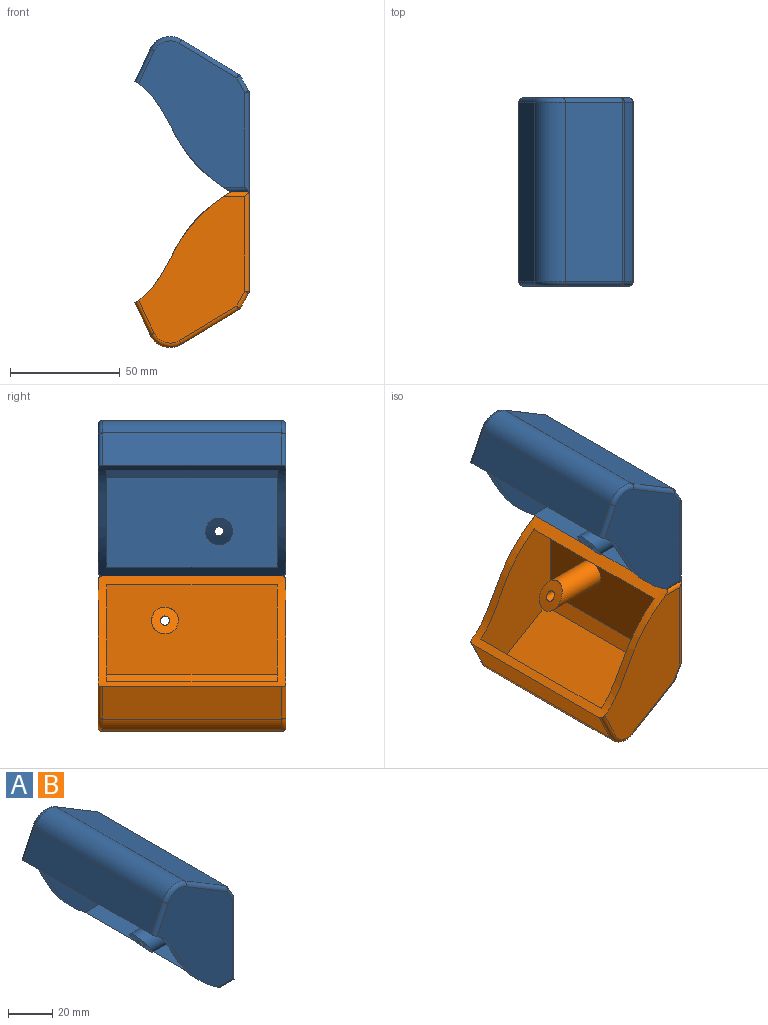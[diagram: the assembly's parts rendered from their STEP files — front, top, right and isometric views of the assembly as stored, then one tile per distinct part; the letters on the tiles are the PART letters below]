
ASSEMBLY  parts=2 mates=1
PART A: 38 faces, bbox 52.8x85.6x72.1 mm
  f0: plane 81.6x6.67mm, normal (0.87,0,0.49), area 624.7mm2, adj f19,f22,f23,f26
  f1: plane 69.24x50.77mm, normal (0,-1,0), area 1975.9mm2, adj f14,f15,f16,f17,f18,f26,f28
  f2: plane 69.24x50.77mm, normal (0,1,0), area 1975.9mm2, adj f9,f10,f11,f12,f13,f19,f28
  f3: plane 81.6x14.69mm, normal (-0.9,0,0.43), area 1328.2mm2, adj f8,f13,f18,f28
  f4: plane 81.6x8.33mm, normal (0,0,-1), area 679.4mm2, adj f5,f12,f17,f28
  f5: plane 81.6x45.27mm, normal (1,0,0), area 3680.4mm2, adj f4,f7,f10,f15,f23
  f6: plane 81.6x26.14mm, normal (0.52,0,0.86), area 2490.6mm2, adj f8,f9,f14,f22
  f7: cylinder r=2.1mm len=31.51mm, axis (1,0,0), area 397.6mm2, adj f5,f27
  f8: cylinder r=10mm len=81.6mm, axis (0,1,0), area 1360.6mm2, adj f3,f6,f11,f16
  f9: cylinder r=2mm len=27.17mm, axis (-0.86,0,0.52), area 95.9mm2, adj f2,f6,f11,f20
  f10: cylinder r=2mm len=45.27mm, axis (0,0,1), area 139.9mm2, adj f2,f5,f12,f21
  f11: torus R=8mm, axis (0,-1,0), area 48.6mm2, adj f2,f8,f9,f13
  f12: cylinder r=2mm len=11.6mm, axis (1,0,0), area 27.7mm2, adj f2,f4,f10,f28
  f13: cylinder r=2mm len=15.74mm, axis (-0.43,0,-0.9), area 51.5mm2, adj f2,f3,f11,f28
  f14: cylinder r=2mm len=27.17mm, axis (0.86,0,-0.52), area 95.9mm2, adj f1,f6,f16,f24
  f15: cylinder r=2mm len=45.27mm, axis (0,0,-1), area 139.9mm2, adj f1,f5,f17,f25
  f16: torus R=8mm, axis (0,-1,0), area 48.6mm2, adj f1,f8,f14,f18
  f17: cylinder r=2mm len=11.6mm, axis (-1,0,0), area 27.7mm2, adj f1,f4,f15,f28
  f18: cylinder r=2mm len=15.74mm, axis (0.43,0,0.9), area 51.5mm2, adj f1,f3,f16,f28
  f19: cylinder r=2mm len=7.65mm, axis (-0.49,0,0.87), area 24mm2, adj f0,f2,f20,f21
  f20: sphere r=2mm, area 2.1mm2, adj f9,f19,f22
  f21: sphere r=2mm, area 2.1mm2, adj f10,f19,f23
  f22: cylinder r=2mm len=81.6mm, axis (0,1,0), area 83.9mm2, adj f0,f6,f20,f24
  f23: cylinder r=2mm len=81.6mm, axis (0,-1,0), area 83.9mm2, adj f0,f5,f21,f25
  f24: sphere r=2mm, area 2.1mm2, adj f14,f22,f26
  f25: sphere r=2mm, area 2.1mm2, adj f15,f23,f26
  f26: cylinder r=2mm len=7.65mm, axis (-0.49,0,0.87), area 24mm2, adj f0,f1,f24,f25
  f27: extruded ~12.2x12.2mm, area 124.6mm2, adj f7,f30
  f28: extruded ~85.6x50.47mm, area 1425.1mm2, adj f1,f2,f3,f4,f12,f13,f17,f18
  f29: cylinder r=6mm len=77.6mm, axis (0,1,0), area 776.3mm2, adj f31,f34,f35,f36
  f30: cylinder r=6.1mm len=29.87mm, axis (1,0,0), area 994.5mm2, adj f27,f32
  f31: plane 77.6x25.69mm, normal (-0.52,0,-0.86), area 2327.7mm2, adj f29,f35,f36,f37
  f32: plane 77.6x40.75mm, normal (-1,0,0), area 3045.1mm2, adj f30,f33,f35,f36,f37
  f33: plane 77.6x10.53mm, normal (0,0,1), area 817.3mm2, adj f28,f32,f35,f36
  f34: plane 77.6x15.21mm, normal (0.9,0,-0.43), area 1308.3mm2, adj f28,f29,f35,f36
  f35: plane 64.75x46.63mm, normal (0,-1,0), area 1740.3mm2, adj f28,f29,f31,f32,f33,f34,f37
  f36: plane 64.75x46.63mm, normal (0,1,0), area 1740.3mm2, adj f28,f29,f31,f32,f33,f34,f37
  f37: plane 77.6x5.75mm, normal (-0.87,0,-0.49), area 512.4mm2, adj f31,f32,f35,f36
PART B: same geometry as A
PLACE A t=(-33.89,38.05,-9.02)mm fixed
PLACE B rot(axis=(1,0,0),180deg) t=(-33.89,-47.55,-9.02)mm
MATE planar A.f4 <-> B.f4  axis (0,0,-1) through (2.26,-4.75,-9.02)mm
